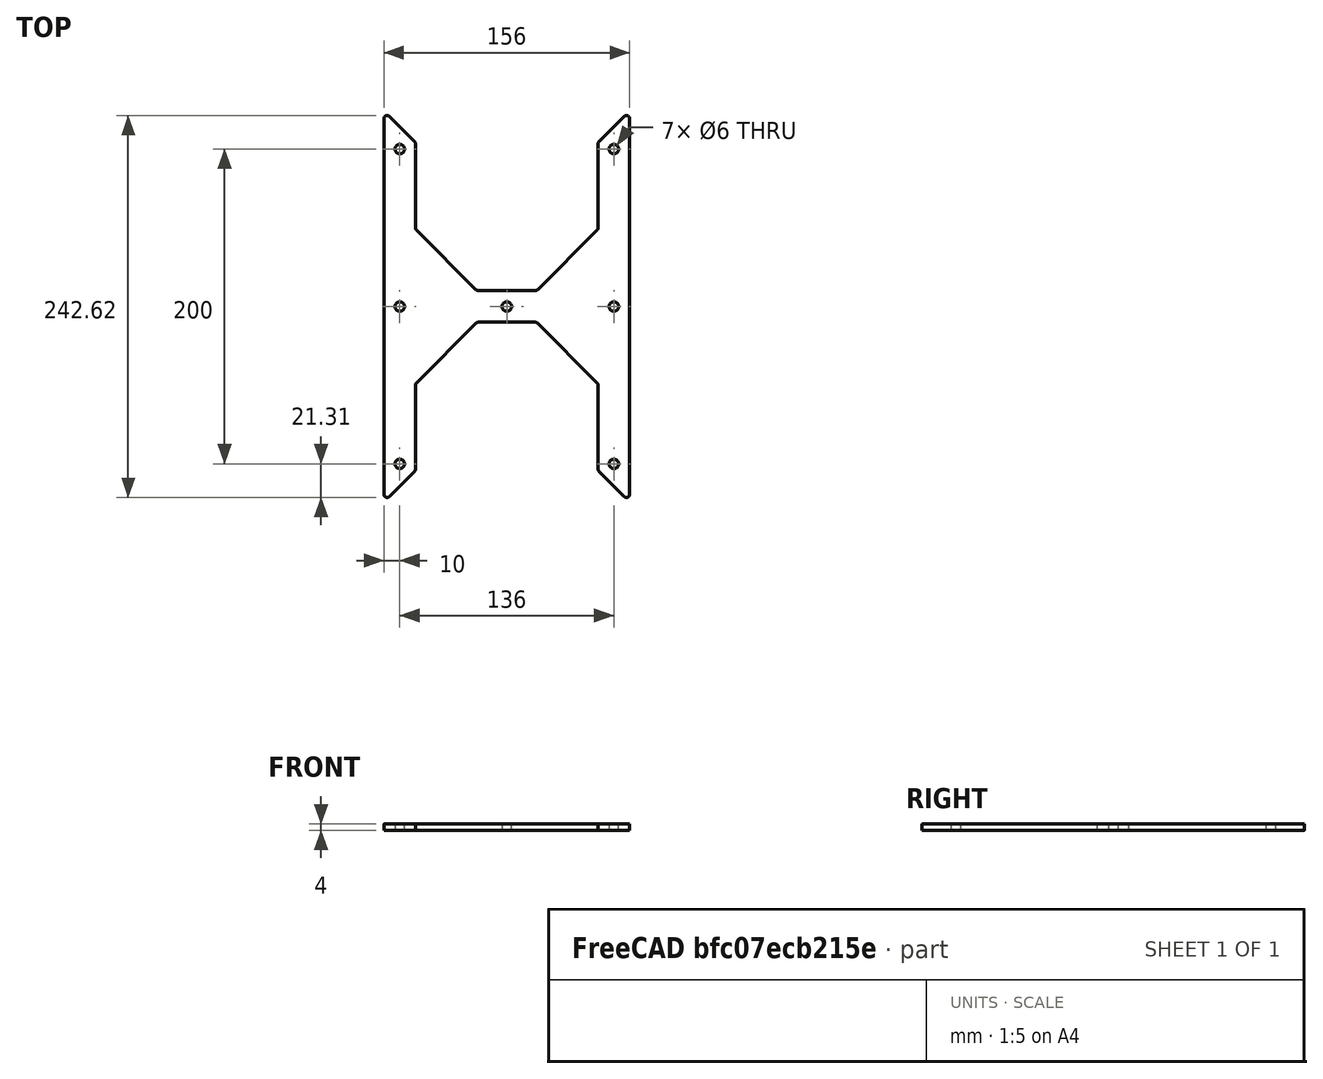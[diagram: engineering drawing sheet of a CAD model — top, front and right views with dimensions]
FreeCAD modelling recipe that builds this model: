
FCSTD DOCUMENT  (FreeCAD 0.19R24267 +99 (Git))
Label: V2 Enclosure middle H bracket
License: All rights reserved
LicenseURL: http://en.wikipedia.org/wiki/All_rights_reserved
objects: Sketcher::SketchObject×1, PartDesign::Pad×1, PartDesign::Body×1
note: 4 computed .brp shape members not serialized (recipe doc carries the construction recipe); baked Part::Feature solids carry a one-line shape summary decoded from their .brp

FEATURE [Sketcher::SketchObject] Sketch
  FullyConstrained = true
  MapMode = 5
  Support = -> [XY_Plane]
  sketch-geometry (45):
    g0: Circle CenterX=-68 CenterY=0 CenterZ=0 NormalX=0 NormalY=0 NormalZ=1 AngleXU=0 Radius=3
    g1: Circle CenterX=68 CenterY=0 CenterZ=0 NormalX=0 NormalY=0 NormalZ=1 AngleXU=0 Radius=3
    g2: LineSegment StartX=-68 StartY=0 StartZ=0 EndX=-68 EndY=-114.142 EndZ=0
    g3: Circle CenterX=-68 CenterY=-100 CenterZ=0 NormalX=0 NormalY=0 NormalZ=1 AngleXU=0 Radius=3
    g4: LineSegment StartX=68 StartY=0 StartZ=0 EndX=68 EndY=-114.142 EndZ=0
    g5: Circle CenterX=68 CenterY=-100 CenterZ=0 NormalX=0 NormalY=0 NormalZ=1 AngleXU=0 Radius=3
    g6: LineSegment StartX=-78 StartY=119.314 StartZ=0 EndX=-78 EndY=-119.314 EndZ=0
    g7: LineSegment StartX=-58 StartY=-50 StartZ=0 EndX=-58 EndY=-103.314 EndZ=0
    g8: LineSegment StartX=-57.4142 StartY=-48.5858 StartZ=0 EndX=-19.4142 EndY=-10.5858 EndZ=0
    g9: LineSegment StartX=-18 StartY=-10 StartZ=0 EndX=18 EndY=-10 EndZ=0
    g10: LineSegment StartX=19.4142 StartY=-10.5858 StartZ=0 EndX=57.4142 EndY=-48.5858 EndZ=0
    g11: LineSegment StartX=58 StartY=-50 StartZ=0 EndX=58 EndY=-103.314 EndZ=0
    g12: LineSegment StartX=58.5858 StartY=-104.728 StartZ=0 EndX=74.5858 EndY=-120.728 EndZ=0
    g13: LineSegment StartX=78 StartY=-119.314 StartZ=0 EndX=78 EndY=119.314 EndZ=0
    g14: LineSegment StartX=18 StartY=10 StartZ=0 EndX=-18 EndY=10 EndZ=0
    g15: LineSegment StartX=-74.5858 StartY=-120.728 StartZ=0 EndX=-58.5858 EndY=-104.728 EndZ=0
    g16: ArcOfCircle CenterX=-76 CenterY=-119.314 CenterZ=0 NormalX=0 NormalY=0 NormalZ=1 AngleXU=0 Radius=2 StartAngle=3.14159 EndAngle=5.49779
    g17: ArcOfCircle CenterX=-60 CenterY=-103.314 CenterZ=0 NormalX=0 NormalY=0 NormalZ=1 AngleXU=0 Radius=2 StartAngle=5.49779 EndAngle=6.28319
    g18: ArcOfCircle CenterX=60 CenterY=-103.314 CenterZ=0 NormalX=0 NormalY=0 NormalZ=1 AngleXU=0 Radius=2 StartAngle=3.14159 EndAngle=3.92699
    g19: ArcOfCircle CenterX=76 CenterY=-119.314 CenterZ=0 NormalX=0 NormalY=0 NormalZ=1 AngleXU=0 Radius=2 StartAngle=3.92699 EndAngle=6.28319
    g20: ArcOfCircle CenterX=-56 CenterY=-50 CenterZ=0 NormalX=0 NormalY=0 NormalZ=1 AngleXU=0 Radius=2 StartAngle=2.35619 EndAngle=3.14159
    g21: ArcOfCircle CenterX=-18 CenterY=-12 CenterZ=0 NormalX=0 NormalY=0 NormalZ=1 AngleXU=0 Radius=2 StartAngle=1.5708 EndAngle=2.35619
    g22: ArcOfCircle CenterX=18 CenterY=-12 CenterZ=0 NormalX=0 NormalY=0 NormalZ=1 AngleXU=0 Radius=2 StartAngle=0.785398 EndAngle=1.5708
    g23: ArcOfCircle CenterX=56 CenterY=-50 CenterZ=0 NormalX=0 NormalY=0 NormalZ=1 AngleXU=0 Radius=2 StartAngle=-9e-16 EndAngle=0.785398
    g24: Circle CenterX=-68 CenterY=-100 CenterZ=0 NormalX=0 NormalY=0 NormalZ=1 AngleXU=0 Radius=10
    g25: Circle CenterX=68 CenterY=-100 CenterZ=0 NormalX=0 NormalY=0 NormalZ=1 AngleXU=0 Radius=10
    g26: GeomPoint X=0 Y=-10 Z=0
    g27: GeomPoint X=0 Y=10 Z=0
    g28: Circle CenterX=0 CenterY=0 CenterZ=0 NormalX=0 NormalY=0 NormalZ=1 AngleXU=0 Radius=3
    g29: LineSegment StartX=-19.4142 StartY=10.5858 StartZ=0 EndX=-57.4142 EndY=48.5858 EndZ=0
    g30: LineSegment StartX=-58 StartY=50 StartZ=0 EndX=-58 EndY=103.314 EndZ=0
    g31: LineSegment StartX=19.4142 StartY=10.5858 StartZ=0 EndX=57.4142 EndY=48.5858 EndZ=0
    g32: LineSegment StartX=58 StartY=50 StartZ=0 EndX=58 EndY=103.314 EndZ=0
    g33: LineSegment StartX=-74.5858 StartY=120.728 StartZ=0 EndX=-58.5858 EndY=104.728 EndZ=0
    g34: LineSegment StartX=58.5858 StartY=104.728 StartZ=0 EndX=74.5858 EndY=120.728 EndZ=0
    g35: ArcOfCircle CenterX=-76 CenterY=119.314 CenterZ=0 NormalX=0 NormalY=0 NormalZ=1 AngleXU=0 Radius=2 StartAngle=0.785398 EndAngle=3.14159
    g36: ArcOfCircle CenterX=-60 CenterY=103.314 CenterZ=0 NormalX=0 NormalY=0 NormalZ=1 AngleXU=0 Radius=2 StartAngle=-9e-16 EndAngle=0.785398
    g37: ArcOfCircle CenterX=-56 CenterY=50 CenterZ=0 NormalX=0 NormalY=0 NormalZ=1 AngleXU=0 Radius=2 StartAngle=3.14159 EndAngle=3.92699
    g38: ArcOfCircle CenterX=-18 CenterY=12 CenterZ=0 NormalX=0 NormalY=0 NormalZ=1 AngleXU=0 Radius=2 StartAngle=3.92699 EndAngle=4.71239
    g39: ArcOfCircle CenterX=18 CenterY=12 CenterZ=0 NormalX=0 NormalY=0 NormalZ=1 AngleXU=0 Radius=2 StartAngle=4.71239 EndAngle=5.49779
    g40: ArcOfCircle CenterX=56 CenterY=50 CenterZ=0 NormalX=0 NormalY=0 NormalZ=1 AngleXU=0 Radius=2 StartAngle=5.49779 EndAngle=6.28319
    g41: ArcOfCircle CenterX=60 CenterY=103.314 CenterZ=0 NormalX=0 NormalY=0 NormalZ=1 AngleXU=0 Radius=2 StartAngle=2.35619 EndAngle=3.14159
    g42: ArcOfCircle CenterX=76 CenterY=119.314 CenterZ=0 NormalX=0 NormalY=0 NormalZ=1 AngleXU=0 Radius=2 StartAngle=-1.8e-15 EndAngle=2.35619
    g43: Circle CenterX=-68 CenterY=100 CenterZ=0 NormalX=0 NormalY=0 NormalZ=1 AngleXU=0 Radius=3
    g44: Circle CenterX=68 CenterY=100 CenterZ=0 NormalX=0 NormalY=0 NormalZ=1 AngleXU=0 Radius=3
  constraints (97):
    c: PointOnObject(g0,g-1)
    c: Symmetric(g0,g1,g-2)
    c: Coincident(g2,g0)
    c: Vertical(g2)
    c: PointOnObject(g3,g2)
    c: Coincident(g4,g1)
    c: Vertical(g4)
    c: Symmetric(g3,g5,g-2)
    c: DistanceX(g0,g1) = 136
    c: Vertical(g7)
    c: Tangent(g6,g16) = -1.5708
    c: Tangent(g15,g16) = -1.5708
    c: Tangent(g7,g17) = 1.5708
    c: Tangent(g15,g17) = -1.5708
    c: Tangent(g11,g18) = -1.5708
    c: Tangent(g12,g18) = -1.5708
    c: Tangent(g13,g19) = -1.5708
    c: Tangent(g12,g19) = -1.5708
    c: Tangent(g8,g20) = 1.5708
    c: Tangent(g7,g20) = -1.5708
    c: Tangent(g8,g21) = 1.5708
    c: Tangent(g9,g21) = 1.5708
    c: Tangent(g10,g22) = 1.5708
    c: Tangent(g9,g22) = 1.5708
    c: Tangent(g10,g23) = 1.5708
    c: Tangent(g11,g23) = 1.5708
    c: Equal(g20,g21)
    c: Equal(g22,g23)
    c: Equal(g23,g19)
    c: Equal(g19,g18)
    c: Equal(g18,g16)
    c: Equal(g16,g17)
    c: PointOnObject(g2,g15)
    c: PointOnObject(g4,g12)
    c: Coincident(g24,g3)
    c: Coincident(g25,g5)
    c: Tangent(g25,g13)
    c: Tangent(g25,g12)
    c: Tangent(g11,g25)
    c: Tangent(g6,g24)
    c: Angle(g15,g6) = 0.785398
    c: DistanceX(g7,g9) = 40
    c: DistanceY(g7,g9) = 40
    c: Symmetric(g9,g9,g-2)
    c: Symmetric(g7,g11,g-2)
    c: DistanceX(g6,g7) = 20
    c: Symmetric(g6,g13,g-2)
    c: Symmetric(g7,g11,g-2)
    c: PointOnObject(g26,g-2)
    c: PointOnObject(g26,g9)
    c: Symmetric(g27,g26,g-1)
    c: DistanceY(g26,g27) = 20
    c: Equal(g1,g0)
    c: DistanceY(g3,g0) = 100
    c: Coincident(g28,g-1)
    c: Radius(g3) = 3
    c: Equal(g3,g0)
    c: Equal(g28,g3)
    c: Equal(g5,g3)
    c: Radius(g16) = 2
    c: Tangent(g33,g35) = 1.5708
    c: Tangent(g6,g35) = -1.5708
    c: Tangent(g33,g36) = 1.5708
    c: Tangent(g30,g36) = -1.5708
    c: Tangent(g30,g37) = 1.5708
    c: Tangent(g29,g37) = 1.5708
    c: Tangent(g14,g38) = 1.5708
    c: Tangent(g29,g38) = 1.5708
    c: Tangent(g14,g39) = 1.5708
    c: Tangent(g31,g39) = -1.5708
    c: Tangent(g31,g40) = -1.5708
    c: Tangent(g32,g40) = -1.5708
    c: Tangent(g32,g41) = 1.5708
    c: Tangent(g34,g41) = 1.5708
    c: Tangent(g34,g42) = 1.5708
    c: Tangent(g13,g42) = -1.5708
    c: Equal(g35,g36)
    c: Equal(g36,g37)
    c: Equal(g37,g38)
    c: Equal(g38,g39)
    c: Equal(g39,g40)
    c: Equal(g40,g41)
    c: Equal(g41,g42)
    c: Equal(g42,g16)
    c: Symmetric(g14,g9,g-1)
    c: Symmetric(g14,g9,g-1)
    c: Symmetric(g7,g30,g-1)
    c: Symmetric(g32,g11,g-1)
    c: Symmetric(g6,g6,g-1)
    c: Symmetric(g13,g13,g-1)
    c: Symmetric(g7,g30,g-1)
    c: Symmetric(g32,g11,g-1)
    c: Equal(g20,g16)
    c: Symmetric(g43,g3,g-1)
    c: Symmetric(g44,g5,g-1)
    c: Equal(g3,g43)
    c: Equal(g43,g44)
FEATURE [PartDesign::Pad] Pad
  Direction = (1,1,1)
  Length = 4
  Length2 = 100
  Profile = -> Sketch
  Type = 0
FEATURE [PartDesign::Body] Body
  Group = -> [Sketch,Pad]
  Origin = -> Origin
  Tip = -> Pad
